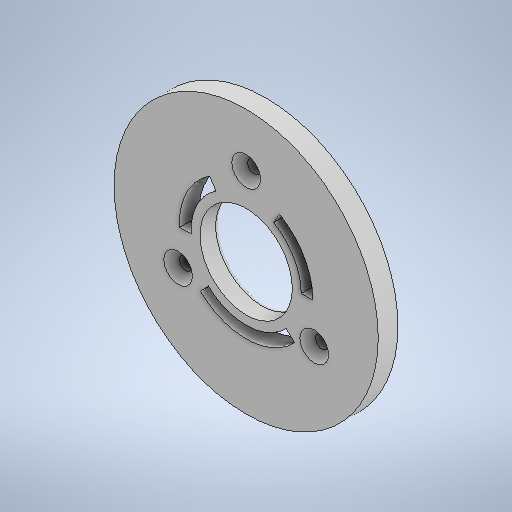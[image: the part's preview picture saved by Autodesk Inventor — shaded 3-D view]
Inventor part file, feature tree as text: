
AUTODESK INVENTOR PART (.ipt)
format: ipt  version: 2025 (Build 290162000, 162)  size: 332,288 bytes
history: native  units: mm
features: sketch x3, extrude x3, fillet x1, chamfer x1
ambient origin geometry x8: Origin, YZ Plane, XZ Plane, XY Plane, X Axis, Y Axis, Z Axis, Center Point
bodies: 实体1 (feature_tree)
feature tree (8):
  sketch  "草图1"  dims[d0=67.2mm d1=40.0mm]
  extrude  "拉伸1"  Depth=40.0mm
  extrude  "拉伸2"  Depth=30.0mm TaperAngle=360.0deg
  extrude  "拉伸3"  Depth=5.0mm TaperAngle=0.0deg
  fillet  "圆角1"  Radius=43.3mm
  chamfer  "倒角1"  Distance=10.3mm
  sketch  "草图 - 环形阵列1"  dims[d2=3.3mm d3=30.0mm d5=360.0deg]
  sketch  "草图 - 环形阵列2"  dims[d7=23.5mm d8=5.0mm d9=0.0mm d10=43.3mm d11=10.3mm d12=160.0mm d14=360.0deg d16=2.0mm d17=0.0mm d18=14.0mm d19=3.0mm d20=45.0deg d21=60.0deg d22=45.0deg d23=5.0mm d24=0.0mm d25=1.0mm d26=2.0mm d27=2.0mm d28=45.0deg]
